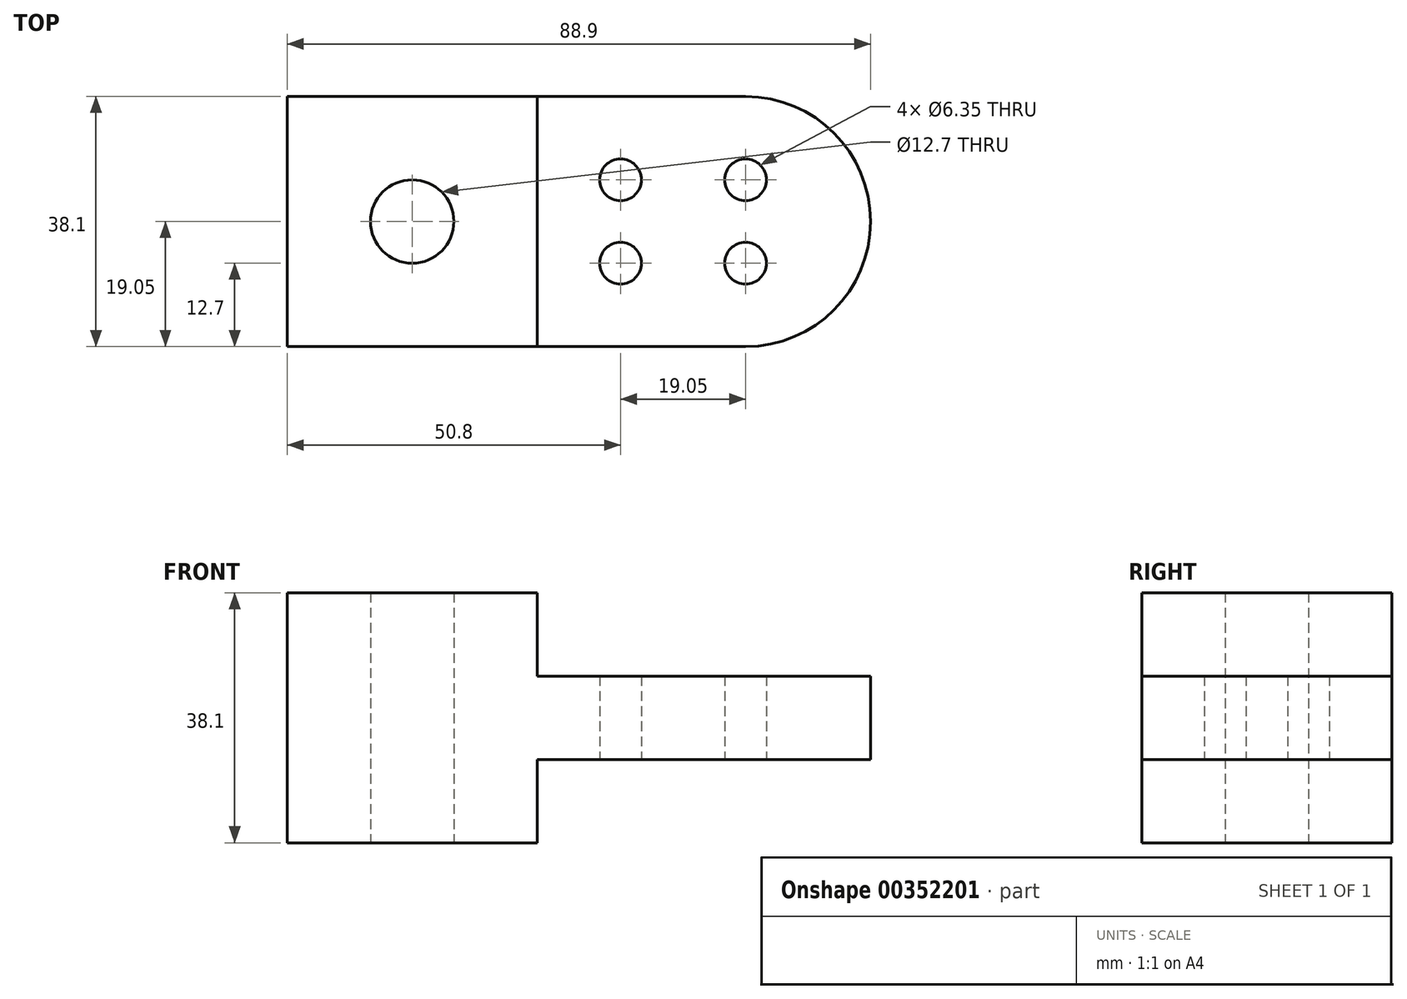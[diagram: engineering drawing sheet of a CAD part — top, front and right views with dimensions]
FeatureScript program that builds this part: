
annotation { "Feature Type Name" : "Feature", "Feature Type Description" : "" }
export const myFeature = defineFeature(function(context is Context, id is Id, definition is map)
    precondition{}
    {
        {
            var Q0;
            Q0=qCreatedBy(makeId("Front.planeOp"),FACE);
            var sketch = newSketch(context, id + "F0", { "sketchPlane" : qUnion([Q0])});
            skLineSegment(sketch, "E0", {"start": v(0, 0) * mm, "end": v(38.1, 0) * mm});
            skLineSegment(sketch, "E1", {"start": v(38.1, 0) * mm, "end": v(38.1, 12.7) * mm});
            skLineSegment(sketch, "E2", {"start": v(38.1, 12.7) * mm, "end": v(88.9, 12.7) * mm});
            skLineSegment(sketch, "E3", {"start": v(88.9, 12.7) * mm, "end": v(88.9, 25.4) * mm});
            skLineSegment(sketch, "E4", {"start": v(88.9, 25.4) * mm, "end": v(38.1, 25.4) * mm});
            skLineSegment(sketch, "E5", {"start": v(38.1, 25.4) * mm, "end": v(38.1, 38.1) * mm});
            skLineSegment(sketch, "E6", {"start": v(38.1, 38.1) * mm, "end": v(0, 38.1) * mm});
            skLineSegment(sketch, "E7", {"start": v(0, 38.1) * mm, "end": v(0, 0) * mm});
            skSolve(sketch);
        }
        {
            var Q0;
            Q0 = qSketchRegion(id + "F0", true);
            extrude(context, id + "F1", {"entities" : qUnion([Q0]), "depth" : 38.1 * mm});
        }
        {
            var Q0;
            Q0=makeQuery(id+"F1.opExtrude","SWEPT_FACE",FACE,{"disambiguationData":[OSD([sQuery(id+"F0.wireOp",EDGE,"E4")])]});
            var sketch = newSketch(context, id + "F2", { "sketchPlane" : qUnion([Q0])});
            skArc(sketch, "E8", {"start": v(69.85, -38.1) * mm, "mid": v(88.9, -19.05) * mm, "end": v(69.85, 0) * mm});
            skLineSegment(sketch, "E9", {"start": v(88.9, 0) * mm, "end": v(88.9, -38.1) * mm});
            skLineSegment(sketch, "E10", {"start": v(69.85, 0) * mm, "end": v(88.9, 0) * mm});
            skLineSegment(sketch, "E11", {"start": v(69.85, -38.1) * mm, "end": v(88.9, -38.1) * mm});
            skSolve(sketch);
        }
        {
            var Q0;
            Q0 = qSketchRegion(id + "F2", true);
            extrude(context, id + "F3", {"entities" : qUnion([Q0]), "operationType" : NewBodyOperationType.REMOVE, "oppositeDirection" : true, "depth" : 25.4 * mm});
        }
        {
            var Q0;
            Q0=qCreatedBy(makeId("Top.planeOp"),FACE);
            var sketch = newSketch(context, id + "F4", { "sketchPlane" : qUnion([Q0])});
            skCircle(sketch, "E12", {"center": v(19.05, -19.05) * mm, "radius": 6.35 * mm});
            skCircle(sketch, "E13", {"center": v(50.8, -12.7) * mm, "radius": 3.18 * mm});
            skCircle(sketch, "E14", {"center": v(50.8, -25.4) * mm, "radius": 3.18 * mm});
            skCircle(sketch, "E15", {"center": v(69.85, -12.7) * mm, "radius": 3.18 * mm});
            skCircle(sketch, "E16", {"center": v(69.85, -25.4) * mm, "radius": 3.18 * mm});
            skSolve(sketch);
        }
        {
            var Q0;
            Q0 = qSketchRegion(id + "F4", true);
            extrude(context, id + "F5", {"entities" : qUnion([Q0]), "operationType" : NewBodyOperationType.REMOVE, "endBound" : BoundingType.THROUGH_ALL, "depth" : 25.4 * mm});
        }
    });
